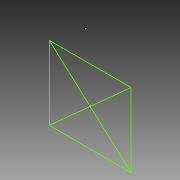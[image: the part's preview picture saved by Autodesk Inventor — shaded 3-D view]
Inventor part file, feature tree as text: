
AUTODESK INVENTOR PART (.ipt)
format: ipt  version: 2012 SP2 (Build 160219200, 219)  size: 164,864 bytes
history: native  units: in
note: dims shown in document units (in); Inventor stores cm internally (conversion verified against a paired STEP export)
features: extrude x6, sketch x6, reference x3, fillet x1
ambient origin geometry x8: Origin, YZ Plane, XZ Plane, XY Plane, X Axis, Y Axis, Z Axis, Center Point
bodies: Solid1 (feature_tree)
feature tree (16):
  extrude  "Extrusion1"  Depth=0.4375in TaperAngle=0.0deg
  extrude  "Extrusion2"  Depth=0.75in TaperAngle=0.0deg
  extrude  "Extrusion3"  Depth=0.25in TaperAngle=0.0deg
  fillet  "Fillet1"  Radius=0.75in
  extrude  "Extrusion4"  [1 undecoded]
  extrude  "Extrusion5"  [1 undecoded]
  extrude  "Extrusion6"  [1 undecoded]
  sketch  "Sketch1"  dims[d0=0.75in d1=0.0in d2=0.4375in d3=0.0in]
  reference  "Reference1"
  sketch  "Sketch2"  dims[d4=0.7874in d6=0.5in d7=0.3937in d9=1.0in d11=0.75in d12=0.0in]
  reference  "Reference2"
  sketch  "Sketch3"  dims[d13=0.6875in d14=0.25in d15=0.0in d16=0.75in d17=0.0in]
  reference  "Reference3"
  sketch  "Sketch4"  dims[d18=0.25in d19=0.0in]
  sketch  "Sketch5"
  sketch  "Sketch6"
note: 3 required parameter values undecoded (feature->parameter linkage not recoverable at this tier; creation-order binding heuristic only, values carry confidence <= 0.55)
